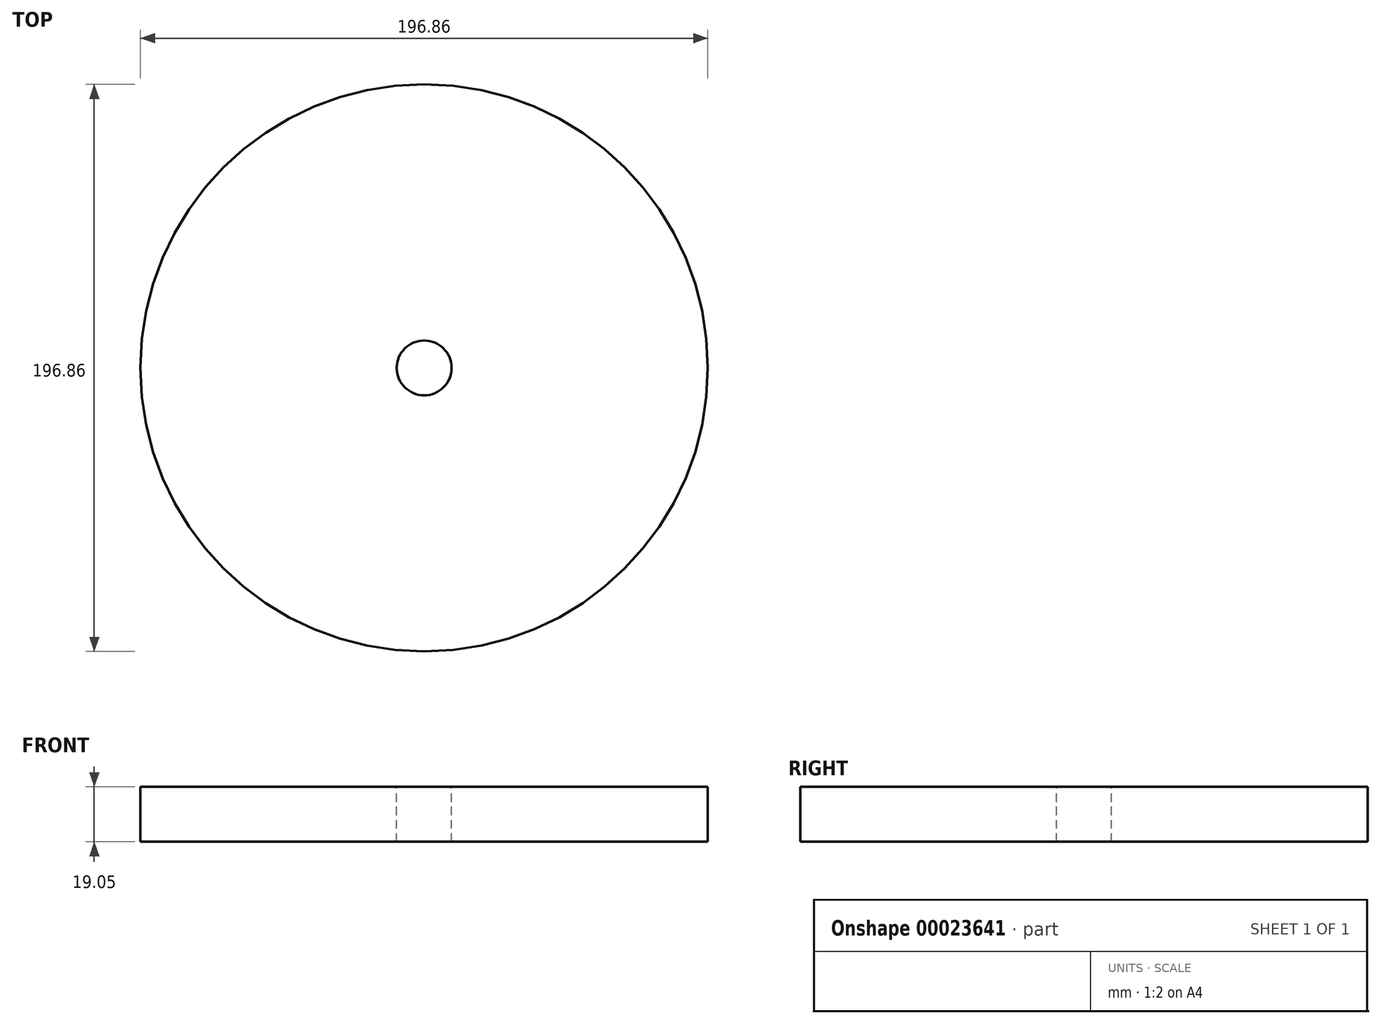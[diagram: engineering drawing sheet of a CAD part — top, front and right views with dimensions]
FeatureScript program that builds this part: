
annotation { "Feature Type Name" : "Feature", "Feature Type Description" : "" }
export const myFeature = defineFeature(function(context is Context, id is Id, definition is map)
    precondition{}
    {
        {
            var Q0;
            Q0=qCreatedBy(makeId("Front.planeOp"),FACE);
            var sketch = newSketch(context, id + "F0", { "sketchPlane" : qUnion([Q0])});
            skLineSegment(sketch, "E0", {"start": v(0, 0) * mm, "end": v(0, 22.77) * mm, "construction": true});
            skLineSegment(sketch, "E1", {"start": v(0, 0) * mm, "end": v(0, -19.64) * mm, "construction": true});
            skLineSegment(sketch, "E2", {"start": v(-9.53, 22.77) * mm, "end": v(-9.53, -19.34) * mm});
            skLineSegment(sketch, "E3.bottom", {"start": v(-9.53, -0.6) * mm, "end": v(-98.42, -0.6) * mm});
            skLineSegment(sketch, "E3.top", {"start": v(-9.53, -19.64) * mm, "end": v(-98.42, -19.64) * mm});
            skLineSegment(sketch, "E3.left", {"start": v(-9.53, -0.6) * mm, "end": v(-9.53, -19.64) * mm});
            skLineSegment(sketch, "E3.right", {"start": v(-98.42, -0.6) * mm, "end": v(-98.42, -19.64) * mm});
            skLineSegment(sketch, "E4.bottom", {"start": v(-9.53, -0.6) * mm, "end": v(-60.33, -0.6) * mm});
            skLineSegment(sketch, "E4.top", {"start": v(-9.53, 56.56) * mm, "end": v(-60.33, 56.56) * mm});
            skLineSegment(sketch, "E4.left", {"start": v(-9.53, -0.6) * mm, "end": v(-9.53, 56.56) * mm});
            skLineSegment(sketch, "E4.right", {"start": v(-60.33, -0.6) * mm, "end": v(-60.33, 56.56) * mm});
            skLineSegment(sketch, "E5.bottom", {"start": v(-9.53, 56.56) * mm, "end": v(-47.63, 56.56) * mm});
            skLineSegment(sketch, "E5.top", {"start": v(-9.53, 69.26) * mm, "end": v(-47.63, 69.26) * mm});
            skLineSegment(sketch, "E5.left", {"start": v(-9.53, 56.56) * mm, "end": v(-9.53, 69.26) * mm});
            skLineSegment(sketch, "E5.right", {"start": v(-47.63, 56.56) * mm, "end": v(-47.63, 69.26) * mm});
            skLineSegment(sketch, "E6", {"start": v(0, 22.77) * mm, "end": v(0, 138.8) * mm, "construction": true});
            skLineSegment(sketch, "E7", {"start": v(0, 138.8) * mm, "end": v(0, -122.95) * mm, "construction": true});
            skSolve(sketch);
        }
        {
            var Q0;
            Q0=makeQuery(id+"F0.imprint","IMPRINT",FACE,{"disambiguationData":[TD([[makeQuery(id+"F0.imprint","IMPRINT",EDGE,{"derivedFrom":sQuery(id+"F0.wireOp",EDGE,"E5.bottom")}),-1.0]])]});
            var Q1;
            {var subQ2=sQuery(id+"F0.wireOp",EDGE,"E4.bottom");Q1=makeQuery(id+"F0.imprint","IMPRINT",FACE,{"disambiguationData":[TD([[makeQuery(id+"F0.imprint","IMPRINT",EDGE,{"derivedFrom":subQ2}),-1.0]])]});}
            var Q2;
            Q2=makeQuery(id+"F0.imprint","IMPRINT",FACE,{"disambiguationData":[TD([[makeQuery(id+"F0.imprint","IMPRINT",EDGE,{"derivedFrom":sQuery(id+"F0.wireOp",EDGE,"E3.bottom")}),1.0]])]});
            var Q3;
            Q3=sQuery(id+"F0.wireOp",EDGE,"E7");
            revolve(context, id + "F1", {"entities" : qUnion([Q0, Q1, Q2]), "axis" : qUnion([Q3]), "revolveType" : RevolveType.FULL});
        }
    });
